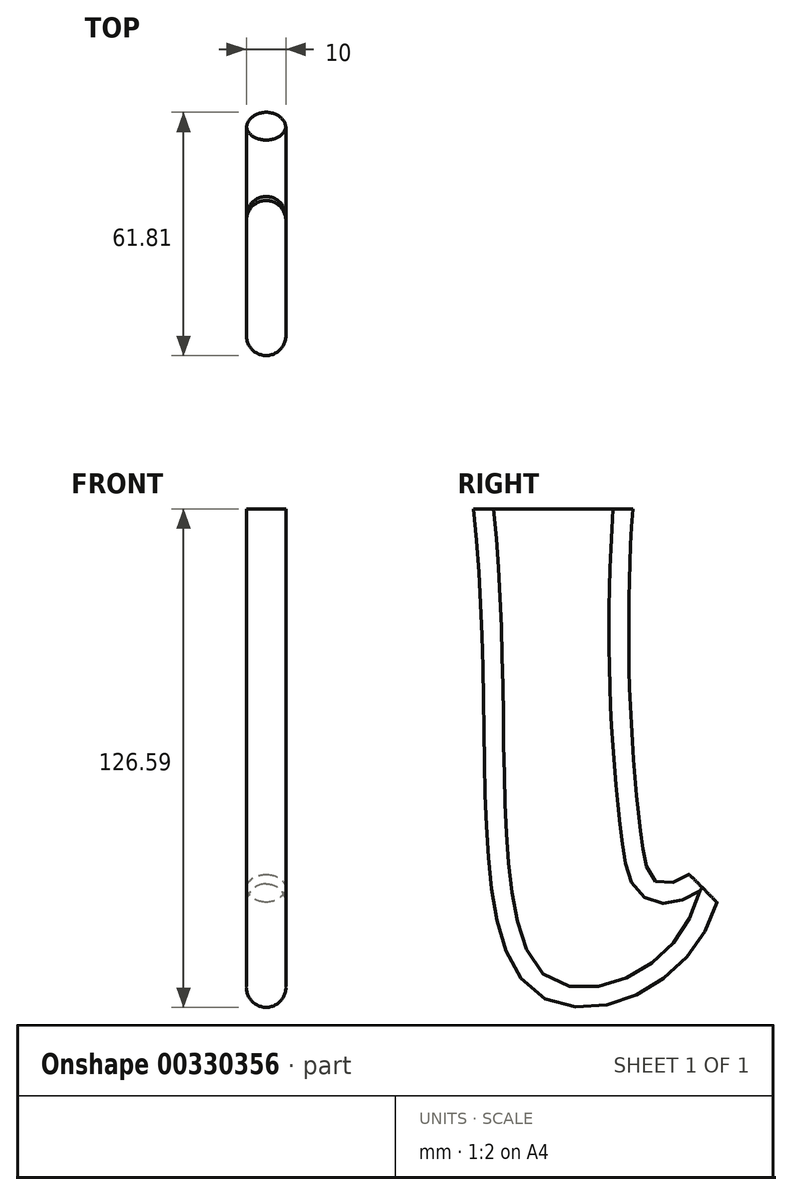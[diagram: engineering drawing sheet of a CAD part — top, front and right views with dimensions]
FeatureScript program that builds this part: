
annotation { "Feature Type Name" : "Feature", "Feature Type Description" : "" }
export const myFeature = defineFeature(function(context is Context, id is Id, definition is map)
    precondition{}
    {
        {
            var Q0;
            Q0=qCreatedBy(makeId("Top.planeOp"),FACE);
            var sketch = newSketch(context, id + "F0", { "sketchPlane" : qUnion([Q0])});
            skLineSegment(sketch, "E0.bottom", {"start": v(50, 50) * mm, "end": v(-50, 50) * mm});
            skLineSegment(sketch, "E0.top", {"start": v(50, -50) * mm, "end": v(-50, -50) * mm});
            skLineSegment(sketch, "E0.left", {"start": v(50, 50) * mm, "end": v(50, -50) * mm});
            skLineSegment(sketch, "E0.right", {"start": v(-50, 50) * mm, "end": v(-50, -50) * mm});
            skPoint(sketch, "E0.middle", {"position": v(0, 0) * mm});
            skSolve(sketch);
        }
        {
            var Q0;
            Q0=qCreatedBy(makeId("Right.planeOp"),FACE);
            var sketch = newSketch(context, id + "F1", { "sketchPlane" : qUnion([Q0])});
            skLineSegment(sketch, "E1", {"start": v(32.93, -92.93) * mm, "end": v(40, -100) * mm});
            skLineSegment(sketch, "E2", {"start": v(40, -100) * mm, "end": v(50, -100) * mm});
            skLineSegment(sketch, "E3", {"start": v(50, -100) * mm, "end": v(50, 0) * mm});
            skLineSegment(sketch, "E4", {"start": v(-21.8, -0.11) * mm, "end": v(18.6, -0.11) * mm});
            skFitSpline(sketch, "E5", {"points": [v(40, -100) * mm, v(-4.77, -123.99) * mm, v(-21.8, -0.11) * mm], "startDerivative": vector(-50.56, -171.74) * mm, "endDerivative": vector(-29.54, 276.57) * mm});
            skFitSpline(sketch, "E6", {"points": [v(32.93, -92.93) * mm, v(20.78, -83.59) * mm, v(18.6, -0.11) * mm], "startDerivative": vector(-99.58, -62.37) * mm, "endDerivative": vector(9.95, 150.07) * mm});
            skSolve(sketch);
        }
        {
            var Q0;
            Q0=sQuery(id+"F1.wireOp",EDGE,"E1");
            extrude(context, id + "F2", {"bodyType" : ToolBodyType.SURFACE, "surfaceEntities" : qUnion([Q0]), "endBound" : BoundingType.SYMMETRIC, "depth" : 10 * mm});
        }
        {
            var Q0;
            Q0=makeQuery(id+"F1.imprint","IMPRINT",FACE,{"disambiguationData":[TD([[makeQuery(id+"F1.imprint","IMPRINT",EDGE,{"derivedFrom":sQuery(id+"F1.wireOp",EDGE,"E1")}),-1.0]])]});
            var Q1;
            Q1=sQuery(id+"F1.wireOp",EDGE,"E6");
            var Q2;
            Q2=sQuery(id+"F1.wireOp",EDGE,"E5");
            var Q3;
            Q3=sQuery(id+"F1.wireOp",EDGE,"E1");
            var Q4;
            Q4=sQuery(id+"F1.wireOp",EDGE,"E4");
            extrude(context, id + "F3", {"entities" : qUnion([Q0]), "surfaceEntities" : qUnion([Q1, Q2, Q3, Q4]), "endBound" : BoundingType.SYMMETRIC, "depth" : 10 * mm});
        }
        {
            var Q0;
            Q0=makeQuery(id+"F3.opExtrude","CAP_EDGE",EDGE,{"disambiguationData":[OSD([sQuery(id+"F1.wireOp",EDGE,"E6")])],"isStart":false});
            var Q1;
            Q1=makeQuery(id+"F3.opExtrude","CAP_EDGE",EDGE,{"disambiguationData":[OSD([sQuery(id+"F1.wireOp",EDGE,"E5")])],"isStart":false});
            var Q2;
            Q2=makeQuery(id+"F3.opExtrude","CAP_EDGE",EDGE,{"disambiguationData":[OSD([sQuery(id+"F1.wireOp",EDGE,"E6")])],"isStart":true});
            var Q3;
            Q3=makeQuery(id+"F3.opExtrude","CAP_EDGE",EDGE,{"disambiguationData":[OSD([sQuery(id+"F1.wireOp",EDGE,"E5")])],"isStart":true});
            fillet(context, id + "F4", {"entities" : qUnion([Q0, Q1, Q2, Q3]), "radius" : 5 * mm, "tangentPropagation" : true, "allowEdgeOverflow" : false});
        }
    });
